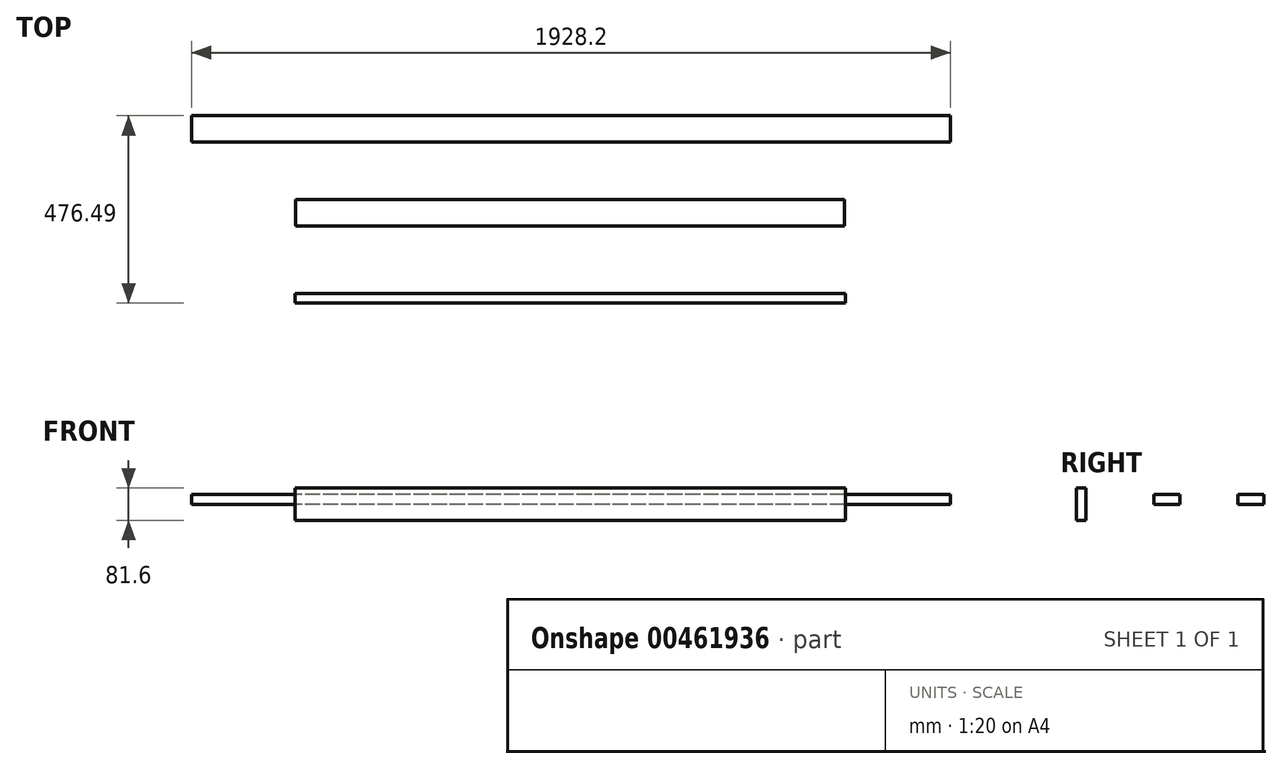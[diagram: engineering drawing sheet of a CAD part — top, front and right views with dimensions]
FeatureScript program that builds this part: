
annotation { "Feature Type Name" : "Feature", "Feature Type Description" : "" }
export const myFeature = defineFeature(function(context is Context, id is Id, definition is map)
    precondition{}
    {
        {
            var Q0;
            Q0=qCreatedBy(makeId("Front.planeOp"),FACE);
            var sketch = newSketch(context, id + "F0", { "sketchPlane" : qUnion([Q0])});
            skLineSegment(sketch, "E0.bottom", {"start": v(698.9, -40.8) * mm, "end": v(-698.9, -40.8) * mm});
            skLineSegment(sketch, "E0.top", {"start": v(698.9, 40.8) * mm, "end": v(-698.9, 40.8) * mm});
            skLineSegment(sketch, "E0.left", {"start": v(698.9, -40.8) * mm, "end": v(698.9, 40.8) * mm});
            skLineSegment(sketch, "E0.right", {"start": v(-698.9, -40.8) * mm, "end": v(-698.9, 40.8) * mm});
            skPoint(sketch, "E0.middle", {"position": v(0, 0) * mm});
            skSolve(sketch);
        }
        {
            var Q0;
            Q0=makeQuery(id+"F0.imprint","IMPRINT",FACE,{"disambiguationData":[TD([[makeQuery(id+"F0.imprint","IMPRINT",EDGE,{"derivedFrom":sQuery(id+"F0.wireOp",EDGE,"E0.bottom")}),-1.0]])]});
            extrude(context, id + "F1", {"entities" : qUnion([Q0]), "depth" : 24.5 * mm});
        }
        {
            var Q0;
            Q0=qCreatedBy(makeId("Top.planeOp"),FACE);
            var sketch = newSketch(context, id + "F2", { "sketchPlane" : qUnion([Q0])});
            skLineSegment(sketch, "E1.bottom", {"start": v(697, 171.9) * mm, "end": v(-697, 171.9) * mm});
            skLineSegment(sketch, "E1.top", {"start": v(697, 238.5) * mm, "end": v(-697, 238.5) * mm});
            skLineSegment(sketch, "E1.left", {"start": v(697, 171.9) * mm, "end": v(697, 238.5) * mm});
            skLineSegment(sketch, "E1.right", {"start": v(-697, 171.9) * mm, "end": v(-697, 238.5) * mm});
            skPoint(sketch, "E1.middle", {"position": v(0, 205.2) * mm});
            skSolve(sketch);
        }
        {
            var Q0;
            Q0=qSketchRegion(id+"F2",true);
            extrude(context, id + "F3", {"entities" : qUnion([Q0]), "depth" : 25 * mm});
        }
        {
            var Q0;
            Q0=qCreatedBy(makeId("Top.planeOp"),FACE);
            var sketch = newSketch(context, id + "F4", { "sketchPlane" : qUnion([Q0])});
            skLineSegment(sketch, "E2.bottom", {"start": v(966.14, 385.4) * mm, "end": v(-962.06, 385.4) * mm});
            skLineSegment(sketch, "E2.top", {"start": v(966.14, 452) * mm, "end": v(-962.06, 452) * mm});
            skLineSegment(sketch, "E2.left", {"start": v(966.14, 385.4) * mm, "end": v(966.14, 452) * mm});
            skLineSegment(sketch, "E2.right", {"start": v(-962.06, 385.4) * mm, "end": v(-962.06, 452) * mm});
            skPoint(sketch, "E2.middle", {"position": v(2.04, 418.7) * mm});
            skSolve(sketch);
        }
        {
            var Q0;
            Q0=qSketchRegion(id+"F4",true);
            extrude(context, id + "F5", {"entities" : qUnion([Q0]), "depth" : 25 * mm});
        }
    });
